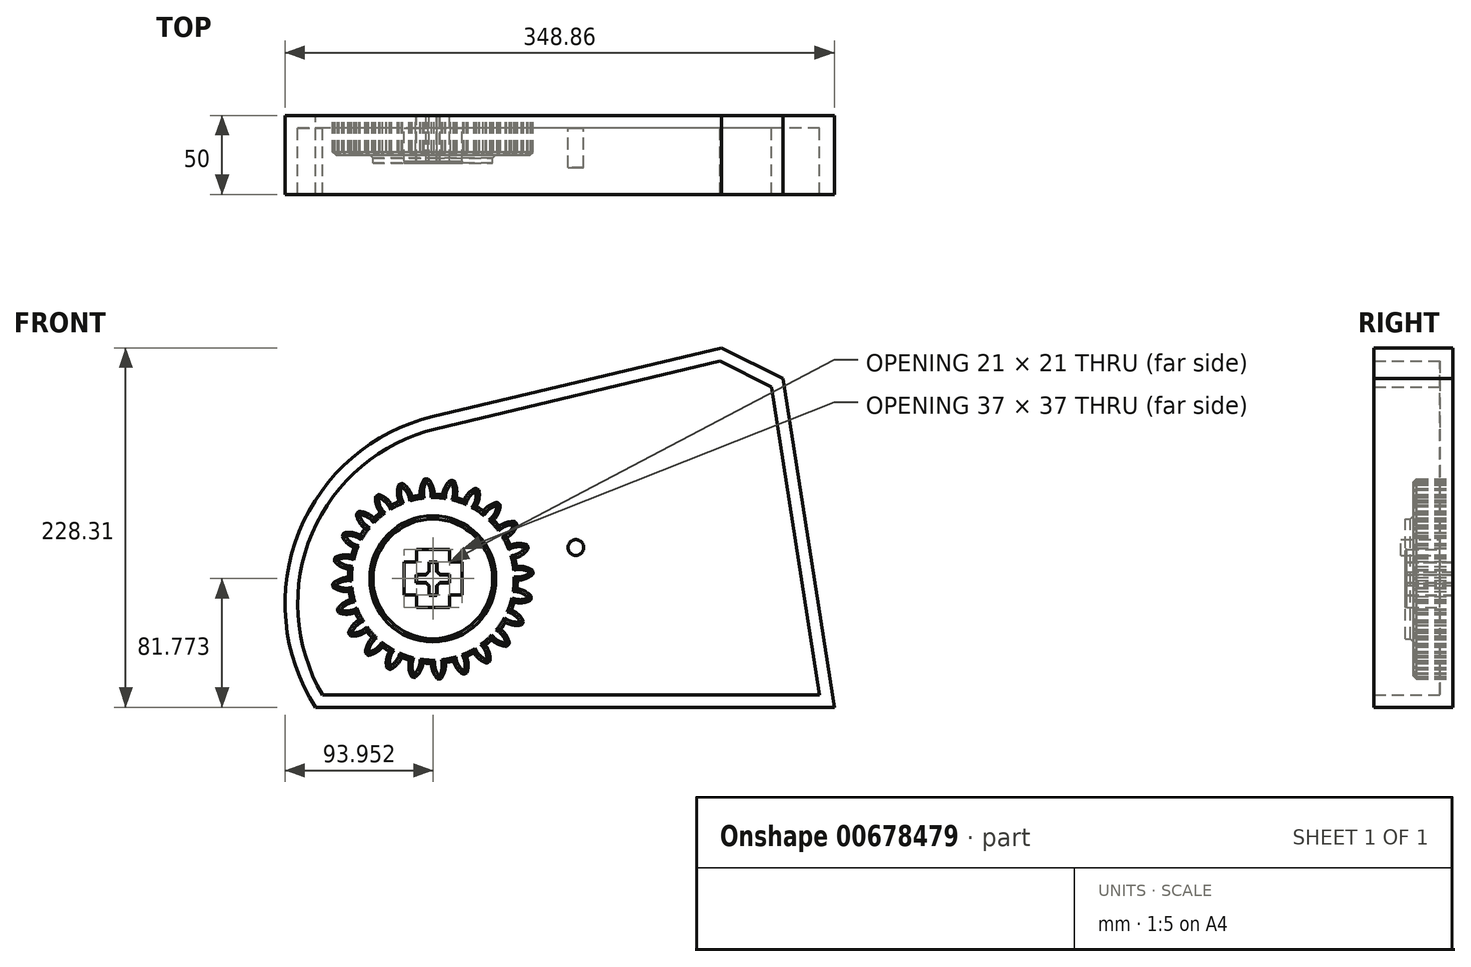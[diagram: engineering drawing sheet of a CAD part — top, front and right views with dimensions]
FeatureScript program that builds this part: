
annotation { "Feature Type Name" : "Feature", "Feature Type Description" : "" }
export const myFeature = defineFeature(function(context is Context, id is Id, definition is map)
    precondition{}
    {
        {
            var Q0;
            Q0=qCreatedBy(makeId("Front.planeOp"),FACE);
            var sketch = newSketch(context, id + "F0", { "sketchPlane" : qUnion([Q0])});
            skCircle(sketch, "E0", {"center": v(0, 0) * mm, "radius": 53.72 * mm});
            skCircle(sketch, "E1", {"center": v(0, 0) * mm, "radius": 58.67 * mm, "construction": true});
            skCircle(sketch, "E2", {"center": v(0, 0) * mm, "radius": 63.5 * mm, "construction": true});
            skLineSegment(sketch, "E3", {"start": v(0, 0) * mm, "end": v(0, 101.5) * mm, "construction": true});
            skLineSegment(sketch, "E4", {"start": v(0, 0) * mm, "end": v(-7.23, 110.28) * mm, "construction": true});
            skLineSegment(sketch, "E5", {"start": v(0, 58.67) * mm, "end": v(-75.03, 58.67) * mm, "construction": true});
            skLineSegment(sketch, "E6", {"start": v(0, 58.67) * mm, "end": v(-75.24, 31.29) * mm, "construction": true});
            skCircle(sketch, "E7", {"center": v(0, 0) * mm, "radius": 55.14 * mm, "construction": true});
            skCircle(sketch, "E8", {"center": v(0, 58.67) * mm, "radius": 14.6 * mm, "construction": true});
            skCircle(sketch, "E9", {"center": v(-13.72, 53.68) * mm, "radius": 14.6 * mm, "construction": true});
            skArc(sketch, "E10", {"start": v(0, 58.67) * mm, "mid": v(-1.2, 61.2) * mm, "end": v(-2.86, 63.44) * mm});
            skArc(sketch, "E11", {"start": v(0.88, 53.71) * mm, "mid": v(0.66, 56.23) * mm, "end": v(0, 58.67) * mm});
            skArc(sketch, "E12.MirrorCS", {"start": v(-7.66, 58.17) * mm, "mid": v(-6.8, 60.82) * mm, "end": v(-5.45, 63.27) * mm});
            skArc(sketch, "E13.MirrorCS", {"start": v(-7.88, 53.14) * mm, "mid": v(-8, 55.67) * mm, "end": v(-7.66, 58.17) * mm});
            skArc(sketch, "E14", {"start": v(-2.86, 63.44) * mm, "mid": v(-4.16, 63.54) * mm, "end": v(-5.45, 63.27) * mm});
            skCircle(sketch, "E15", {"center": v(0, 0) * mm, "radius": 38 * mm});
            skLineSegment(sketch, "E16.bottom", {"start": v(-2.5, -10.5) * mm, "end": v(2.5, -10.5) * mm});
            skLineSegment(sketch, "E16.top", {"start": v(-2.5, 10.5) * mm, "end": v(2.5, 10.5) * mm});
            skLineSegment(sketch, "E16.left", {"start": v(-2.5, -10.5) * mm, "end": v(-2.5, 10.5) * mm});
            skLineSegment(sketch, "E16.right", {"start": v(2.5, -10.5) * mm, "end": v(2.5, 10.5) * mm});
            skLineSegment(sketch, "E17.bottom", {"start": v(-10.5, -2.5) * mm, "end": v(10.5, -2.5) * mm});
            skLineSegment(sketch, "E17.top", {"start": v(-10.5, 2.5) * mm, "end": v(10.5, 2.5) * mm});
            skLineSegment(sketch, "E17.left", {"start": v(-10.5, -2.5) * mm, "end": v(-10.5, 2.5) * mm});
            skLineSegment(sketch, "E17.right", {"start": v(10.5, -2.5) * mm, "end": v(10.5, 2.5) * mm});
            skCircle(sketch, "E18", {"center": v(0, 0) * mm, "radius": 5 * mm});
            skSolve(sketch);
        }
        {
            var Q0;
            {var subQ0=sQuery(id+"F0.wireOp",EDGE,"E0");var subQ1=makeQuery(id+"F0.imprint","INTERSECT",VERTEX,{"derivedFrom":[subQ0,sQuery(id+"F0.wireOp",EDGE,"E11")]});Q0=makeQuery(id+"F0.imprint","IMPRINT",FACE,{"disambiguationData":[TD([[makeQuery(id+"F0.imprint","IMPRINT",EDGE,{"disambiguationData":[TD([[subQ1,-1.0]])],"derivedFrom":subQ0}),1.0]])]});}
            var Q1;
            Q1=makeQuery(id+"F0.imprint","IMPRINT",FACE,{"disambiguationData":[TD([[makeQuery(id+"F0.imprint","IMPRINT",EDGE,{"derivedFrom":sQuery(id+"F0.wireOp",EDGE,"E10")}),1.0]])]});
            extrude(context, id + "F1", {"entities" : qUnion([Q0, Q1]), "depth" : 25 * mm, "offsetDistance" : 25 * mm});
        }
        {
            var Q0;
            Q0=makeQuery(id+"F1.opExtrude","SWEPT_BODY",BODY,{"disambiguationData":[OSD([sQuery(id+"F0.wireOp",EDGE,"E0"),sQuery(id+"F0.wireOp",EDGE,"E10"),sQuery(id+"F0.wireOp",EDGE,"E11"),sQuery(id+"F0.wireOp",EDGE,"E12.MirrorCS"),sQuery(id+"F0.wireOp",EDGE,"E13.MirrorCS"),sQuery(id+"F0.wireOp",EDGE,"E14")])]});
            var Q1;
            Q1=makeQuery(id+"F1.opExtrude","SWEPT_FACE",FACE,{"disambiguationData":[OSD([sQuery(id+"F0.wireOp",EDGE,"E0")])]});
            circularPattern(context, id + "F2", {"entities" : qUnion([Q0]), "axis" : qUnion([Q1]), "angle" : 360 * degree, "instanceCount" : 24, "equalSpace" : true});
        }
        {
            var Q0;
            Q0=makeQuery(id+"F0.imprint","IMPRINT",FACE,{"disambiguationData":[TD([[makeQuery(id+"F0.imprint","IMPRINT",EDGE,{"derivedFrom":sQuery(id+"F0.wireOp",EDGE,"E15")}),1.0]])]});
            extrude(context, id + "F3", {"entities" : qUnion([Q0]), "operationType" : NewBodyOperationType.ADD, "depth" : 30 * mm, "offsetDistance" : 25 * mm});
        }
        {
            var Q0;
            {var subQ0=makeQuery(id+"F1.opExtrude","CAP_FACE",FACE,{"disambiguationData":[OSD([sQuery(id+"F0.wireOp",EDGE,"E0"),sQuery(id+"F0.wireOp",EDGE,"E10"),sQuery(id+"F0.wireOp",EDGE,"E11"),sQuery(id+"F0.wireOp",EDGE,"E12.MirrorCS"),sQuery(id+"F0.wireOp",EDGE,"E13.MirrorCS"),sQuery(id+"F0.wireOp",EDGE,"E14"),sQuery(id+"F0.wireOp",EDGE,"E15")])],"isStart":false});Q0=makeQuery(id+"F3.boolean.opBoolean","MERGE",FACE,{"derivedFrom":[subQ0,makeQuery(id+"F2.opPattern","COPY",FACE,{"derivedFrom":subQ0,"instanceName":"1"}),makeQuery(id+"F2.opPattern","COPY",FACE,{"derivedFrom":subQ0,"instanceName":"2"}),makeQuery(id+"F2.opPattern","COPY",FACE,{"derivedFrom":subQ0,"instanceName":"3"}),makeQuery(id+"F2.opPattern","COPY",FACE,{"derivedFrom":subQ0,"instanceName":"4"}),makeQuery(id+"F2.opPattern","COPY",FACE,{"derivedFrom":subQ0,"instanceName":"5"}),makeQuery(id+"F2.opPattern","COPY",FACE,{"derivedFrom":subQ0,"instanceName":"6"}),makeQuery(id+"F2.opPattern","COPY",FACE,{"derivedFrom":subQ0,"instanceName":"7"}),makeQuery(id+"F2.opPattern","COPY",FACE,{"derivedFrom":subQ0,"instanceName":"8"}),makeQuery(id+"F2.opPattern","COPY",FACE,{"derivedFrom":subQ0,"instanceName":"9"}),makeQuery(id+"F2.opPattern","COPY",FACE,{"derivedFrom":subQ0,"instanceName":"10"}),makeQuery(id+"F2.opPattern","COPY",FACE,{"derivedFrom":subQ0,"instanceName":"11"}),makeQuery(id+"F2.opPattern","COPY",FACE,{"derivedFrom":subQ0,"instanceName":"12"}),makeQuery(id+"F2.opPattern","COPY",FACE,{"derivedFrom":subQ0,"instanceName":"13"}),makeQuery(id+"F2.opPattern","COPY",FACE,{"derivedFrom":subQ0,"instanceName":"14"}),makeQuery(id+"F2.opPattern","COPY",FACE,{"derivedFrom":subQ0,"instanceName":"15"}),makeQuery(id+"F2.opPattern","COPY",FACE,{"derivedFrom":subQ0,"instanceName":"16"}),makeQuery(id+"F2.opPattern","COPY",FACE,{"derivedFrom":subQ0,"instanceName":"17"}),makeQuery(id+"F2.opPattern","COPY",FACE,{"derivedFrom":subQ0,"instanceName":"18"}),makeQuery(id+"F2.opPattern","COPY",FACE,{"derivedFrom":subQ0,"instanceName":"19"}),makeQuery(id+"F2.opPattern","COPY",FACE,{"derivedFrom":subQ0,"instanceName":"20"}),makeQuery(id+"F2.opPattern","COPY",FACE,{"derivedFrom":subQ0,"instanceName":"21"}),makeQuery(id+"F2.opPattern","COPY",FACE,{"derivedFrom":subQ0,"instanceName":"22"}),makeQuery(id+"F2.opPattern","COPY",FACE,{"derivedFrom":subQ0,"instanceName":"23"})]});}
            chamfer(context, id + "F4", {"entities" : qUnion([Q0]), "width" : 2 * mm, "tangentPropagation" : true});
        }
        {
            var Q0;
            Q0=qCreatedBy(makeId("Front.planeOp"),FACE);
            var sketch = newSketch(context, id + "F5", { "sketchPlane" : qUnion([Q0])});
            skLineSegment(sketch, "E19", {"start": v(255.04, -81.57) * mm, "end": v(222.29, 127.22) * mm});
            skLineSegment(sketch, "E20", {"start": v(222.29, 127.22) * mm, "end": v(183.25, 146.74) * mm});
            skLineSegment(sketch, "E21", {"start": v(183.25, 146.74) * mm, "end": v(0, 103.03) * mm});
            skLineSegment(sketch, "E22", {"start": v(255.04, -81.57) * mm, "end": v(-74.6, -81.57) * mm});
            skArc(sketch, "E23", {"start": v(0, 103.03) * mm, "mid": v(-84.92, 29.97) * mm, "end": v(-74.6, -81.57) * mm});
            skSolve(sketch);
        }
        {
            var Q0;
            Q0=makeQuery(id+"F5.imprint","IMPRINT",FACE,{"disambiguationData":[TD([[makeQuery(id+"F5.imprint","IMPRINT",EDGE,{"derivedFrom":sQuery(id+"F5.wireOp",EDGE,"E19")}),1.0]])]});
            var sketch = newSketch(context, id + "F6", { "sketchPlane" : qUnion([Q0])});
            skLineSegment(sketch, "E24.bottom", {"start": v(-2.37, -10.3) * mm, "end": v(2.63, -10.3) * mm});
            skLineSegment(sketch, "E24.top", {"start": v(-2.37, 10.7) * mm, "end": v(2.63, 10.7) * mm});
            skLineSegment(sketch, "E24.left", {"start": v(-2.37, -10.3) * mm, "end": v(-2.37, 10.7) * mm});
            skLineSegment(sketch, "E24.right", {"start": v(2.63, -10.3) * mm, "end": v(2.63, 10.7) * mm});
            skLineSegment(sketch, "E25.bottom", {"start": v(-10.37, -2.3) * mm, "end": v(10.63, -2.3) * mm});
            skLineSegment(sketch, "E25.top", {"start": v(-10.37, 2.7) * mm, "end": v(10.63, 2.7) * mm});
            skLineSegment(sketch, "E25.left", {"start": v(-10.37, -2.3) * mm, "end": v(-10.37, 2.7) * mm});
            skLineSegment(sketch, "E25.right", {"start": v(10.63, -2.3) * mm, "end": v(10.63, 2.7) * mm});
            skCircle(sketch, "E26", {"center": v(0.13, 0.2) * mm, "radius": 5 * mm});
            skSolve(sketch);
        }
        {
            var Q0;
            {var subQ7=sQuery(id+"F6.wireOp",EDGE,"E24.bottom");Q0=makeQuery(id+"F6.imprint","IMPRINT",FACE,{"disambiguationData":[TD([[makeQuery(id+"F6.imprint","IMPRINT",EDGE,{"derivedFrom":subQ7}),-1.0]])]});}
            extrude(context, id + "F7", {"entities" : qUnion([Q0]), "depth" : 50 * mm, "offsetDistance" : 25 * mm});
        }
        {
            var Q0;
            Q0=makeQuery(id+"F7.opExtrude","CAP_FACE",FACE,{"disambiguationData":[OSD([sQuery(id+"F5.wireOp",EDGE,"E19"),sQuery(id+"F5.wireOp",EDGE,"E20"),sQuery(id+"F5.wireOp",EDGE,"E21"),sQuery(id+"F5.wireOp",EDGE,"E22"),sQuery(id+"F5.wireOp",EDGE,"E23")])],"isStart":false});
            shell(context, id + "F8", {"entities" : qUnion([Q0]), "thickness" : 8 * mm});
        }
        {
            var Q0;
            {var subQ0=sQuery(id+"F6.wireOp",EDGE,"E26");var subQ1=sQuery(id+"F6.wireOp",EDGE,"E25.right");var subQ2=sQuery(id+"F6.wireOp",EDGE,"E25.left");var subQ3=sQuery(id+"F6.wireOp",EDGE,"E25.top");var subQ4=sQuery(id+"F6.wireOp",EDGE,"E25.bottom");var subQ5=sQuery(id+"F6.wireOp",EDGE,"E24.right");var subQ6=sQuery(id+"F6.wireOp",EDGE,"E24.left");var subQ7=sQuery(id+"F6.wireOp",EDGE,"E24.top");var subQ8=sQuery(id+"F6.wireOp",EDGE,"E24.bottom");var subQ9=sQuery(id+"F5.wireOp",EDGE,"E23");var subQ10=sQuery(id+"F5.wireOp",EDGE,"E22");var subQ11=sQuery(id+"F5.wireOp",EDGE,"E21");var subQ12=sQuery(id+"F5.wireOp",EDGE,"E20");var subQ13=sQuery(id+"F5.wireOp",EDGE,"E19");Q0=makeQuery(id+"F8.opShell","OFFSET_FACE",FACE,{"disambiguationData":[OSD([subQ13,subQ12,subQ11,subQ10,subQ9,subQ8,subQ7,subQ6,subQ5,subQ4,subQ3,subQ2,subQ1,subQ0]),TDD([makeQuery(id+"F7.opExtrude","CAP_FACE",FACE,{"disambiguationData":[OSD([subQ13,subQ12,subQ11,subQ10,subQ9,subQ8,subQ7,subQ6,subQ5,subQ4,subQ3,subQ2,subQ1,subQ0])],"isStart":false})])]});}
            extrude(context, id + "F9", {"entities" : qUnion([Q0]), "operationType" : NewBodyOperationType.REMOVE, "oppositeDirection" : true, "depth" : 21 * mm, "offsetDistance" : 25 * mm});
        }
        {
            var Q0;
            {var subQ0=sQuery(id+"F6.wireOp",EDGE,"E26");var subQ1=sQuery(id+"F6.wireOp",EDGE,"E25.right");var subQ2=sQuery(id+"F6.wireOp",EDGE,"E25.left");var subQ3=sQuery(id+"F6.wireOp",EDGE,"E25.top");var subQ4=sQuery(id+"F6.wireOp",EDGE,"E25.bottom");var subQ5=sQuery(id+"F6.wireOp",EDGE,"E24.right");var subQ6=sQuery(id+"F6.wireOp",EDGE,"E24.left");var subQ7=sQuery(id+"F6.wireOp",EDGE,"E24.top");var subQ8=sQuery(id+"F6.wireOp",EDGE,"E24.bottom");var subQ9=sQuery(id+"F5.wireOp",EDGE,"E23");var subQ10=sQuery(id+"F5.wireOp",EDGE,"E22");var subQ11=sQuery(id+"F5.wireOp",EDGE,"E21");var subQ12=sQuery(id+"F5.wireOp",EDGE,"E20");var subQ13=sQuery(id+"F5.wireOp",EDGE,"E19");Q0=makeQuery(id+"F8.opShell","OFFSET_FACE",FACE,{"disambiguationData":[OSD([subQ13,subQ12,subQ11,subQ10,subQ9,subQ8,subQ7,subQ6,subQ5,subQ4,subQ3,subQ2,subQ1,subQ0]),TDD([makeQuery(id+"F7.opExtrude","CAP_FACE",FACE,{"disambiguationData":[OSD([subQ13,subQ12,subQ11,subQ10,subQ9,subQ8,subQ7,subQ6,subQ5,subQ4,subQ3,subQ2,subQ1,subQ0])],"isStart":true})])]});}
            var sketch = newSketch(context, id + "F10", { "sketchPlane" : qUnion([Q0])});
            skCircle(sketch, "E27", {"center": v(90.82, 19.9) * mm, "radius": 27.57 * mm, "construction": true});
            skCircle(sketch, "E28", {"center": v(90.82, 19.9) * mm, "radius": 29.34 * mm, "construction": true});
            skCircle(sketch, "E29", {"center": v(90.82, 19.9) * mm, "radius": 31.75 * mm, "construction": true});
            skCircle(sketch, "E30", {"center": v(90.82, 19.9) * mm, "radius": 26.86 * mm});
            skCircle(sketch, "E31", {"center": v(62.48, 12.3) * mm, "radius": 14.6 * mm, "construction": true});
            skLineSegment(sketch, "E32", {"start": v(90.82, 19.9) * mm, "end": v(37.6, 5.63) * mm, "construction": true});
            skLineSegment(sketch, "E33", {"start": v(90.82, 19.9) * mm, "end": v(36.78, 1.55) * mm, "construction": true});
            skCircle(sketch, "E34", {"center": v(71.17, 0.56) * mm, "radius": 14.6 * mm, "construction": true});
            skLineSegment(sketch, "E35", {"start": v(62.48, 12.3) * mm, "end": v(73.36, -28.29) * mm, "construction": true});
            skLineSegment(sketch, "E36", {"start": v(62.48, 12.3) * mm, "end": v(85.86, -21.08) * mm, "construction": true});
            skArc(sketch, "E37.MirrorCS", {"start": v(62.14, 6.29) * mm, "mid": v(59.35, 6.43) * mm, "end": v(56.65, 7.1) * mm});
            skArc(sketch, "E38.MirrorCS", {"start": v(67.06, 7.37) * mm, "mid": v(64.65, 6.61) * mm, "end": v(62.14, 6.29) * mm});
            skArc(sketch, "E39.MirrorCS", {"start": v(59.78, 13.23) * mm, "mid": v(57.66, 11.42) * mm, "end": v(55.92, 9.24) * mm});
            skArc(sketch, "E40.MirrorCS", {"start": v(64.34, 15.36) * mm, "mid": v(61.97, 14.5) * mm, "end": v(59.78, 13.23) * mm});
            skArc(sketch, "E41", {"start": v(55.92, 9.24) * mm, "mid": v(55.87, 8.03) * mm, "end": v(56.65, 7.1) * mm});
            skCircle(sketch, "E42", {"center": v(90.82, 19.9) * mm, "radius": 5 * mm});
            skLineSegment(sketch, "E43.0", {"start": v(90.82, 19.9) * mm, "end": v(62.48, 12.3) * mm, "construction": true});
            skSolve(sketch);
        }
        {
            var Q0;
            Q0=makeQuery(id+"F10.imprint","IMPRINT",FACE,{"disambiguationData":[TD([[makeQuery(id+"F10.imprint","IMPRINT",EDGE,{"derivedFrom":sQuery(id+"F10.wireOp",EDGE,"E42")}),1.0]])]});
            extrude(context, id + "F11", {"entities" : qUnion([Q0]), "operationType" : NewBodyOperationType.ADD, "depth" : 25 * mm, "offsetDistance" : 25 * mm});
        }
    });
